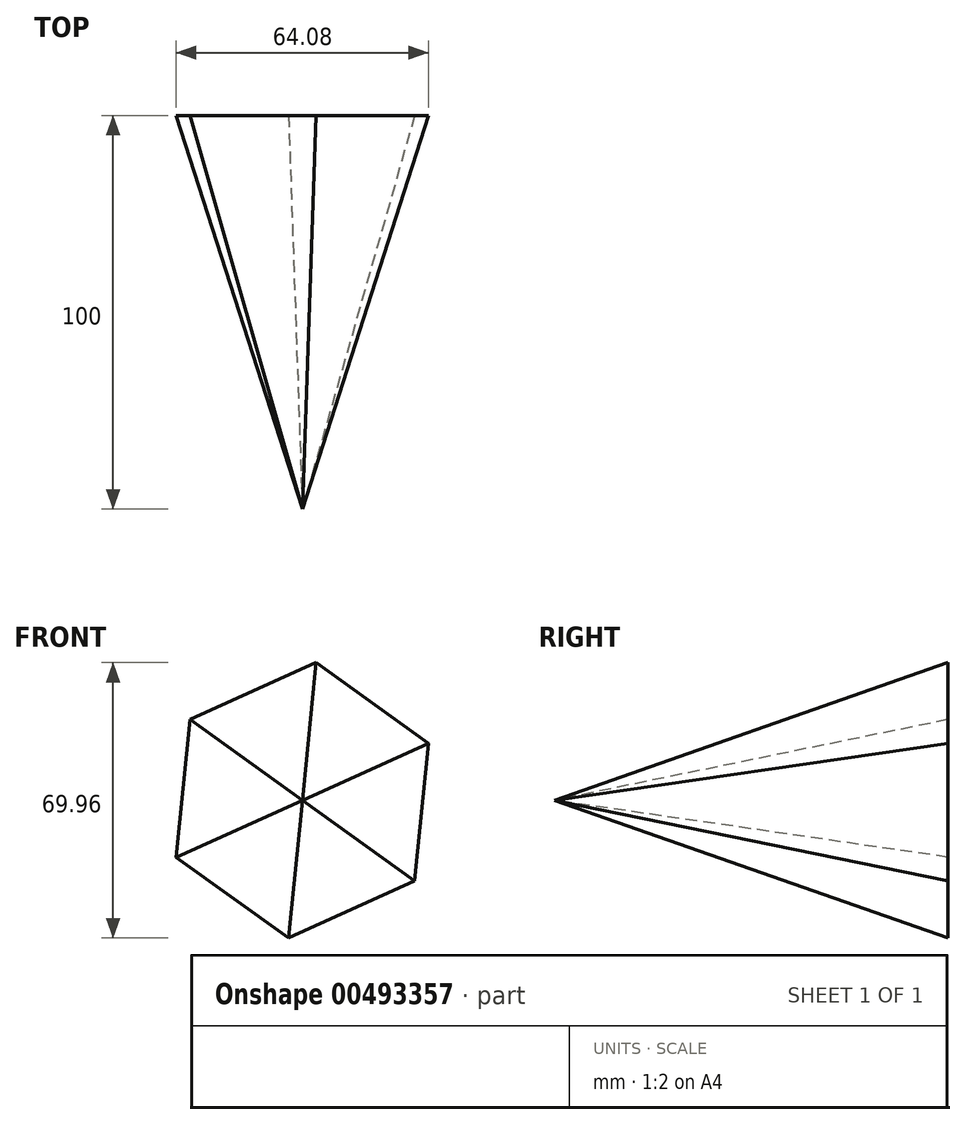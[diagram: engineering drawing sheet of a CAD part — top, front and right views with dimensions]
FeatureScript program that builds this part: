
annotation { "Feature Type Name" : "Feature", "Feature Type Description" : "" }
export const myFeature = defineFeature(function(context is Context, id is Id, definition is map)
    precondition{}
    {
        {
            var Q0;
            Q0=qCreatedBy(makeId("Front.planeOp"),FACE);
            var sketch = newSketch(context, id + "F0", { "sketchPlane" : qUnion([Q0])});
            skCircle(sketch, "E0.cCircle", {"center": v(0, 0) * mm, "radius": 35.15 * mm, "construction": true});
            skLineSegment(sketch, "E0.0", {"start": v(-28.55, 20.51) * mm, "end": v(3.5, 34.98) * mm});
            skLineSegment(sketch, "E0.1", {"start": v(3.5, 34.98) * mm, "end": v(32.04, 14.46) * mm});
            skLineSegment(sketch, "E0.2", {"start": v(32.04, 14.46) * mm, "end": v(28.55, -20.51) * mm});
            skLineSegment(sketch, "E0.3", {"start": v(28.55, -20.51) * mm, "end": v(-3.5, -34.98) * mm});
            skLineSegment(sketch, "E0.4", {"start": v(-3.5, -34.98) * mm, "end": v(-32.04, -14.46) * mm});
            skLineSegment(sketch, "E0.5", {"start": v(-32.04, -14.46) * mm, "end": v(-28.55, 20.51) * mm});
            skSolve(sketch);
        }
        {
            var Q0;
            Q0=qCreatedBy(makeId("Front.planeOp"),FACE);
            cPlane(context, id + "F1", {"entities" : qUnion([Q0]), "cplaneType" : CPlaneType.OFFSET, "offset" : 100 * mm, "width" : 150 * mm, "height" : 150 * mm});
        }
        {
            var Q0;
            Q0=qCreatedBy(id+"F1.planeOp",FACE);
            var sketch = newSketch(context, id + "F2", { "sketchPlane" : qUnion([Q0])});
            skPoint(sketch, "E1", {"position": v(0, 0) * mm});
            skSolve(sketch);
        }
        {
            var Q0;
            Q0=makeQuery(id+"F0.imprint","IMPRINT",FACE,{"disambiguationData":[TD([[makeQuery(id+"F0.imprint","IMPRINT",EDGE,{"derivedFrom":sQuery(id+"F0.wireOp",EDGE,"E0.0")}),-1.0]])]});
            var Q1;
            Q1=sQuery(id+"F2.wireOp",VERTEX,"E1");
            loft(context, id + "F3", {"sheetProfilesArray" : [{ "sheetProfileEntities" : qUnion([Q0]) }, { "sheetProfileEntities" : qUnion([Q1]) }]});
        }
    });
